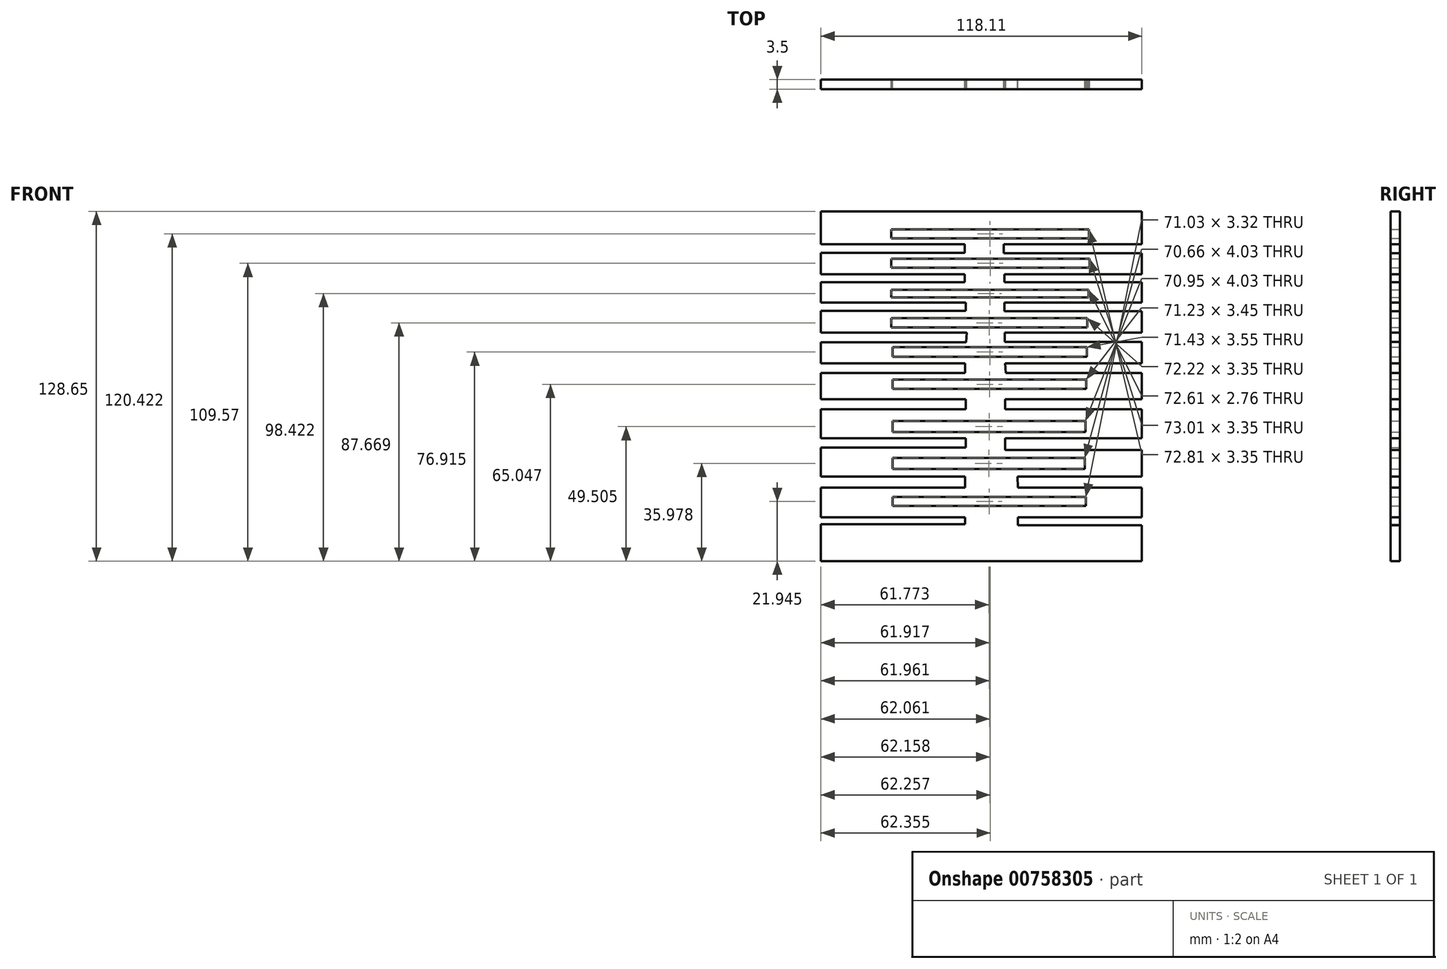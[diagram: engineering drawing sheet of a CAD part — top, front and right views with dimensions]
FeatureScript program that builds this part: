
annotation { "Feature Type Name" : "Feature", "Feature Type Description" : "" }
export const myFeature = defineFeature(function(context is Context, id is Id, definition is map)
    precondition{}
    {
        {
            var Q0;
            Q0=qCreatedBy(makeId("Front.planeOp"),FACE);
            var sketch = newSketch(context, id + "F0", { "sketchPlane" : qUnion([Q0])});
            skLineSegment(sketch, "E0.bottom", {"start": v(-61.27, 59.43) * mm, "end": v(56.84, 59.43) * mm});
            skLineSegment(sketch, "E0.top", {"start": v(-61.27, -69.22) * mm, "end": v(56.84, -69.22) * mm});
            skLineSegment(sketch, "E0.left", {"start": v(-61.27, 59.43) * mm, "end": v(-61.27, 47.35) * mm});
            skLineSegment(sketch, "E0.right", {"start": v(56.84, 59.43) * mm, "end": v(56.84, 47.35) * mm});
            skLineSegment(sketch, "E1.bottom", {"start": v(-34.83, -45.62) * mm, "end": v(36.2, -45.62) * mm});
            skLineSegment(sketch, "E1.top", {"start": v(-34.83, -48.93) * mm, "end": v(36.2, -48.93) * mm});
            skLineSegment(sketch, "E1.left", {"start": v(-34.83, -45.62) * mm, "end": v(-34.83, -48.93) * mm});
            skLineSegment(sketch, "E1.right", {"start": v(36.2, -45.62) * mm, "end": v(36.2, -48.93) * mm});
            skLineSegment(sketch, "E2.bottom", {"start": v(56.84, -38.13) * mm, "end": v(11.08, -38.13) * mm});
            skLineSegment(sketch, "E2.top", {"start": v(56.84, -42.16) * mm, "end": v(11.2, -42.16) * mm});
            skLineSegment(sketch, "E2.right", {"start": v(11.08, -38.13) * mm, "end": v(11.2, -42.16) * mm});
            skLineSegment(sketch, "E3.bottom", {"start": v(-61.27, -38.13) * mm, "end": v(-8.2, -38.13) * mm});
            skLineSegment(sketch, "E3.top", {"start": v(-61.27, -42.16) * mm, "end": v(-8.2, -42.16) * mm});
            skLineSegment(sketch, "E3.right", {"start": v(-8.2, -38.13) * mm, "end": v(-8.2, -42.16) * mm});
            skLineSegment(sketch, "E4.trimOffspring", {"start": v(-61.27, -42.16) * mm, "end": v(-61.27, -53.08) * mm});
            skLineSegment(sketch, "E5.trimOffspring", {"start": v(56.84, -42.16) * mm, "end": v(56.84, -53.08) * mm});
            skLineSegment(sketch, "E6.bottom", {"start": v(-34.83, -31.23) * mm, "end": v(35.83, -31.23) * mm});
            skLineSegment(sketch, "E6.top", {"start": v(-34.83, -35.26) * mm, "end": v(35.83, -35.26) * mm});
            skLineSegment(sketch, "E6.left", {"start": v(-34.83, -31.23) * mm, "end": v(-34.83, -35.26) * mm});
            skLineSegment(sketch, "E6.right", {"start": v(35.83, -31.23) * mm, "end": v(35.83, -35.26) * mm});
            skLineSegment(sketch, "E7.bottom", {"start": v(56.84, -24.03) * mm, "end": v(6.48, -24.03) * mm});
            skLineSegment(sketch, "E7.top", {"start": v(56.84, -28.35) * mm, "end": v(6.48, -28.35) * mm});
            skLineSegment(sketch, "E7.right", {"start": v(6.48, -24.03) * mm, "end": v(6.48, -28.35) * mm});
            skLineSegment(sketch, "E8.bottom", {"start": v(-61.27, -24.03) * mm, "end": v(-7.91, -24.03) * mm});
            skLineSegment(sketch, "E8.top", {"start": v(-61.27, -27.49) * mm, "end": v(-7.91, -27.49) * mm});
            skLineSegment(sketch, "E8.right", {"start": v(-7.91, -24.03) * mm, "end": v(-7.91, -27.49) * mm});
            skLineSegment(sketch, "E9.bottom", {"start": v(-34.83, -17.7) * mm, "end": v(36.12, -17.7) * mm});
            skLineSegment(sketch, "E9.top", {"start": v(-34.83, -21.73) * mm, "end": v(36.12, -21.73) * mm});
            skLineSegment(sketch, "E9.left", {"start": v(-34.83, -17.7) * mm, "end": v(-34.83, -21.73) * mm});
            skLineSegment(sketch, "E9.right", {"start": v(36.12, -17.7) * mm, "end": v(36.12, -21.73) * mm});
            skLineSegment(sketch, "E10.bottom", {"start": v(-7.91, -9.64) * mm, "end": v(-61.27, -9.64) * mm});
            skLineSegment(sketch, "E10.top", {"start": v(-7.91, -13.38) * mm, "end": v(-61.27, -13.38) * mm});
            skLineSegment(sketch, "E10.left", {"start": v(-7.91, -9.64) * mm, "end": v(-7.91, -13.38) * mm});
            skLineSegment(sketch, "E11.bottom", {"start": v(6.48, -9.64) * mm, "end": v(56.84, -9.64) * mm});
            skLineSegment(sketch, "E11.top", {"start": v(6.48, -13.38) * mm, "end": v(56.84, -13.38) * mm});
            skLineSegment(sketch, "E11.left", {"start": v(6.48, -9.64) * mm, "end": v(6.48, -13.38) * mm});
            skLineSegment(sketch, "E12.trimOffspring", {"start": v(-61.27, -13.38) * mm, "end": v(-61.27, -24.03) * mm});
            skLineSegment(sketch, "E13.trimOffspring", {"start": v(56.84, -13.38) * mm, "end": v(56.84, -24.03) * mm});
            skLineSegment(sketch, "E14.bottom", {"start": v(-34.83, -2.45) * mm, "end": v(36.4, -2.45) * mm});
            skLineSegment(sketch, "E14.top", {"start": v(-34.83, -5.9) * mm, "end": v(36.4, -5.9) * mm});
            skLineSegment(sketch, "E14.left", {"start": v(-34.83, -2.45) * mm, "end": v(-34.83, -5.9) * mm});
            skLineSegment(sketch, "E14.right", {"start": v(36.4, -2.45) * mm, "end": v(36.4, -5.9) * mm});
            skLineSegment(sketch, "E15.bottom", {"start": v(-61.27, 3.6) * mm, "end": v(-8.2, 3.6) * mm});
            skLineSegment(sketch, "E15.top", {"start": v(-61.27, 0) * mm, "end": v(-8.2, 0) * mm});
            skLineSegment(sketch, "E15.right", {"start": v(-8.2, 3.6) * mm, "end": v(-8.2, 0) * mm});
            skLineSegment(sketch, "E16.trimOffspring", {"start": v(-61.27, 0) * mm, "end": v(-61.27, -9.64) * mm});
            skLineSegment(sketch, "E17.bottom", {"start": v(56.84, 3.6) * mm, "end": v(6.48, 3.6) * mm});
            skLineSegment(sketch, "E17.top", {"start": v(56.84, 0) * mm, "end": v(6.76, 0) * mm});
            skLineSegment(sketch, "E17.right", {"start": v(6.48, 3.6) * mm, "end": v(6.76, 0) * mm});
            skLineSegment(sketch, "E18.trimOffspring", {"start": v(56.84, 0) * mm, "end": v(56.84, -9.64) * mm});
            skLineSegment(sketch, "E19.trimOffspring", {"start": v(56.84, -28.35) * mm, "end": v(56.84, -38.13) * mm});
            skLineSegment(sketch, "E20.trimOffspring", {"start": v(-61.27, -27.49) * mm, "end": v(-61.27, -38.13) * mm});
            skLineSegment(sketch, "E21.bottom", {"start": v(-34.83, 9.47) * mm, "end": v(36.6, 9.47) * mm});
            skLineSegment(sketch, "E21.top", {"start": v(-34.83, 5.92) * mm, "end": v(36.6, 5.92) * mm});
            skLineSegment(sketch, "E21.left", {"start": v(-34.83, 9.47) * mm, "end": v(-34.83, 5.92) * mm});
            skLineSegment(sketch, "E21.right", {"start": v(36.6, 9.47) * mm, "end": v(36.6, 5.92) * mm});
            skLineSegment(sketch, "E22.bottom", {"start": v(-61.27, 14.8) * mm, "end": v(-7.6, 14.8) * mm});
            skLineSegment(sketch, "E22.top", {"start": v(-61.27, 11.25) * mm, "end": v(-7.8, 11.25) * mm});
            skLineSegment(sketch, "E22.right", {"start": v(-7.6, 14.8) * mm, "end": v(-7.8, 11.25) * mm});
            skLineSegment(sketch, "E23.trimOffspring", {"start": v(-61.27, 11.25) * mm, "end": v(-61.27, 3.6) * mm});
            skLineSegment(sketch, "E24.bottom", {"start": v(56.84, 14.8) * mm, "end": v(6.41, 14.8) * mm});
            skLineSegment(sketch, "E24.top", {"start": v(56.84, 11.44) * mm, "end": v(6.41, 11.44) * mm});
            skLineSegment(sketch, "E24.right", {"start": v(6.41, 14.8) * mm, "end": v(6.41, 11.44) * mm});
            skLineSegment(sketch, "E25.trimOffspring", {"start": v(56.84, 11.44) * mm, "end": v(56.84, 3.6) * mm});
            skLineSegment(sketch, "E26.bottom", {"start": v(-35.42, 20.13) * mm, "end": v(36.8, 20.13) * mm});
            skLineSegment(sketch, "E26.top", {"start": v(-35.42, 16.77) * mm, "end": v(36.8, 16.77) * mm});
            skLineSegment(sketch, "E26.left", {"start": v(-35.42, 20.13) * mm, "end": v(-35.42, 16.77) * mm});
            skLineSegment(sketch, "E26.right", {"start": v(36.8, 20.13) * mm, "end": v(36.8, 16.77) * mm});
            skLineSegment(sketch, "E27.bottom", {"start": v(-61.27, 25.85) * mm, "end": v(-8, 25.85) * mm});
            skLineSegment(sketch, "E27.top", {"start": v(-61.27, 22.89) * mm, "end": v(-8, 22.89) * mm});
            skLineSegment(sketch, "E27.right", {"start": v(-8, 25.85) * mm, "end": v(-8, 22.89) * mm});
            skLineSegment(sketch, "E28.trimOffspring", {"start": v(-61.27, 22.89) * mm, "end": v(-61.27, 14.8) * mm});
            skLineSegment(sketch, "E29.bottom", {"start": v(56.84, 25.85) * mm, "end": v(6.22, 25.85) * mm});
            skLineSegment(sketch, "E29.top", {"start": v(56.84, 22.7) * mm, "end": v(6.22, 22.7) * mm});
            skLineSegment(sketch, "E29.right", {"start": v(6.22, 25.85) * mm, "end": v(6.22, 22.7) * mm});
            skLineSegment(sketch, "E30.trimOffspring", {"start": v(56.84, 22.7) * mm, "end": v(56.84, 14.8) * mm});
            skLineSegment(sketch, "E31.bottom", {"start": v(-35.42, 30.58) * mm, "end": v(37.2, 30.58) * mm});
            skLineSegment(sketch, "E31.top", {"start": v(-35.42, 27.82) * mm, "end": v(37.2, 27.82) * mm});
            skLineSegment(sketch, "E31.left", {"start": v(-35.42, 30.58) * mm, "end": v(-35.42, 27.82) * mm});
            skLineSegment(sketch, "E31.right", {"start": v(37.2, 30.58) * mm, "end": v(37.2, 27.82) * mm});
            skLineSegment(sketch, "E32.bottom", {"start": v(-61.27, 36.3) * mm, "end": v(-8.39, 36.3) * mm});
            skLineSegment(sketch, "E32.top", {"start": v(-61.27, 33.35) * mm, "end": v(-8.39, 33.35) * mm});
            skLineSegment(sketch, "E32.right", {"start": v(-8.39, 36.3) * mm, "end": v(-8.39, 33.35) * mm});
            skLineSegment(sketch, "E33.trimOffspring", {"start": v(-61.27, 33.35) * mm, "end": v(-61.27, 25.85) * mm});
            skLineSegment(sketch, "E34.bottom", {"start": v(56.84, 36.3) * mm, "end": v(6.22, 36.3) * mm});
            skLineSegment(sketch, "E34.top", {"start": v(56.84, 33.35) * mm, "end": v(6.22, 33.35) * mm});
            skLineSegment(sketch, "E34.right", {"start": v(6.22, 36.3) * mm, "end": v(6.22, 33.35) * mm});
            skLineSegment(sketch, "E35.trimOffspring", {"start": v(56.84, 33.35) * mm, "end": v(56.84, 25.85) * mm});
            skLineSegment(sketch, "E36.bottom", {"start": v(-35.42, 42.03) * mm, "end": v(37.59, 42.03) * mm});
            skLineSegment(sketch, "E36.top", {"start": v(-35.42, 38.67) * mm, "end": v(37.59, 38.67) * mm});
            skLineSegment(sketch, "E36.left", {"start": v(-35.42, 42.03) * mm, "end": v(-35.42, 38.67) * mm});
            skLineSegment(sketch, "E36.right", {"start": v(37.59, 42.03) * mm, "end": v(37.59, 38.67) * mm});
            skLineSegment(sketch, "E37.bottom", {"start": v(-61.27, 47.35) * mm, "end": v(-8.39, 47.35) * mm});
            skLineSegment(sketch, "E37.top", {"start": v(-61.27, 44.2) * mm, "end": v(-8.39, 44.2) * mm});
            skLineSegment(sketch, "E37.right", {"start": v(-8.39, 47.35) * mm, "end": v(-8.39, 44.2) * mm});
            skLineSegment(sketch, "E38.trimOffspring", {"start": v(-61.27, 44.2) * mm, "end": v(-61.27, 36.3) * mm});
            skLineSegment(sketch, "E39.bottom", {"start": v(56.84, 47.35) * mm, "end": v(6.02, 47.35) * mm});
            skLineSegment(sketch, "E39.top", {"start": v(56.84, 44) * mm, "end": v(6.02, 44) * mm});
            skLineSegment(sketch, "E39.right", {"start": v(6.02, 47.35) * mm, "end": v(6.02, 44) * mm});
            skLineSegment(sketch, "E40.trimOffspring", {"start": v(56.84, 44) * mm, "end": v(56.84, 36.3) * mm});
            skLineSegment(sketch, "E41.bottom", {"start": v(-35.42, 52.88) * mm, "end": v(37.4, 52.88) * mm});
            skLineSegment(sketch, "E41.top", {"start": v(-35.42, 49.53) * mm, "end": v(37.4, 49.53) * mm});
            skLineSegment(sketch, "E41.left", {"start": v(-35.42, 52.88) * mm, "end": v(-35.42, 49.53) * mm});
            skLineSegment(sketch, "E41.right", {"start": v(37.4, 52.88) * mm, "end": v(37.4, 49.53) * mm});
            skLineSegment(sketch, "E42.bottom", {"start": v(-8.2, -53.08) * mm, "end": v(-61.27, -53.08) * mm});
            skLineSegment(sketch, "E42.top", {"start": v(-8.2, -55.7) * mm, "end": v(-61.27, -55.7) * mm});
            skLineSegment(sketch, "E42.left", {"start": v(-8.2, -53.08) * mm, "end": v(-8.2, -55.7) * mm});
            skLineSegment(sketch, "E43.bottom", {"start": v(56.84, -53.08) * mm, "end": v(11.2, -53.08) * mm});
            skLineSegment(sketch, "E43.top", {"start": v(56.84, -56.04) * mm, "end": v(11.2, -56.04) * mm});
            skLineSegment(sketch, "E43.right", {"start": v(11.2, -53.08) * mm, "end": v(11.2, -56.04) * mm});
            skLineSegment(sketch, "E44.trimOffspring", {"start": v(-61.27, -55.7) * mm, "end": v(-61.27, -69.22) * mm});
            skLineSegment(sketch, "E45.trimOffspring", {"start": v(56.84, -56.04) * mm, "end": v(56.84, -69.22) * mm});
            skSolve(sketch);
        }
        {
            var Q0;
            Q0=makeQuery(id+"F0.imprint","IMPRINT",FACE,{"disambiguationData":[TD([[makeQuery(id+"F0.imprint","IMPRINT",EDGE,{"derivedFrom":sQuery(id+"F0.wireOp",EDGE,"E0.bottom")}),-1.0]])]});
            extrude(context, id + "F1", {"entities" : qUnion([Q0]), "depth" : 3.5 * mm, "offsetDistance" : 25.4 * mm});
        }
    });
